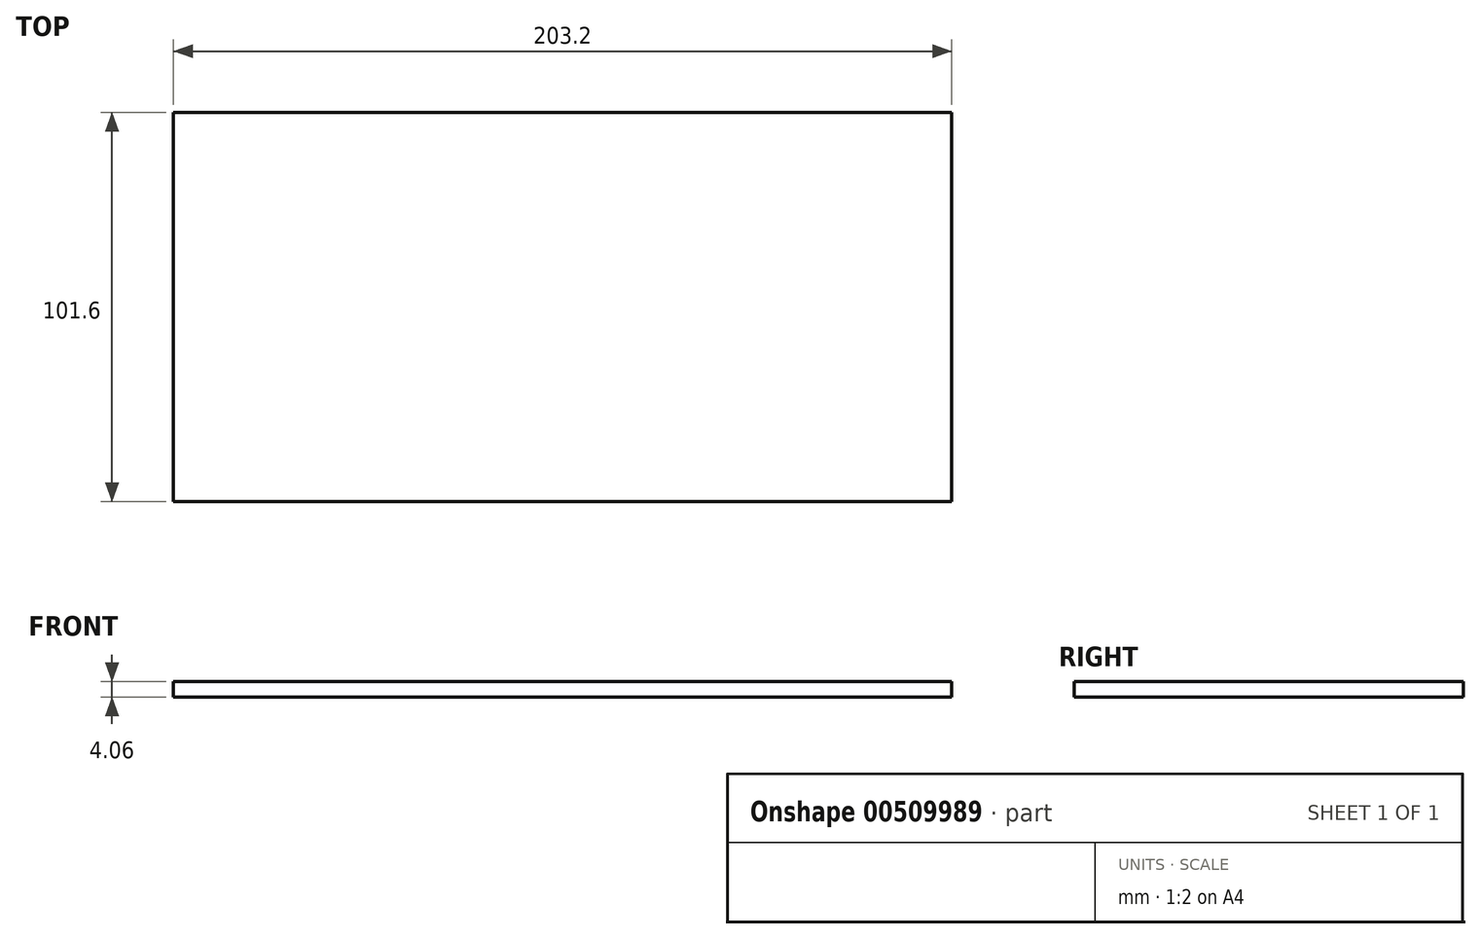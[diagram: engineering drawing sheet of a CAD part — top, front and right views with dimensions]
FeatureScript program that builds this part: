
annotation { "Feature Type Name" : "Feature", "Feature Type Description" : "" }
export const myFeature = defineFeature(function(context is Context, id is Id, definition is map)
    precondition{}
    {
        {
            var Q0;
            Q0=qCreatedBy(makeId("Top.planeOp"),FACE);
            var sketch = newSketch(context, id + "F0", { "sketchPlane" : qUnion([Q0])});
            skLineSegment(sketch, "E0.bottom", {"start": v(-104.1, 101.6) * mm, "end": v(99.1, 101.6) * mm});
            skLineSegment(sketch, "E0.top", {"start": v(-104.1, 0) * mm, "end": v(99.1, 0) * mm});
            skLineSegment(sketch, "E0.left", {"start": v(-104.1, 101.6) * mm, "end": v(-104.1, 0) * mm});
            skLineSegment(sketch, "E0.right", {"start": v(99.1, 101.6) * mm, "end": v(99.1, 0) * mm});
            skSolve(sketch);
        }
        {
            var Q0;
            Q0=makeQuery(id+"F0.imprint","IMPRINT",FACE,{"disambiguationData":[TD([[makeQuery(id+"F0.imprint","IMPRINT",EDGE,{"derivedFrom":sQuery(id+"F0.wireOp",EDGE,"E0.bottom")}),-1.0]])]});
            extrude(context, id + "F1", {"entities" : qUnion([Q0]), "depth" : 4.06 * mm, "offsetDistance" : 25.4 * mm});
        }
    });
